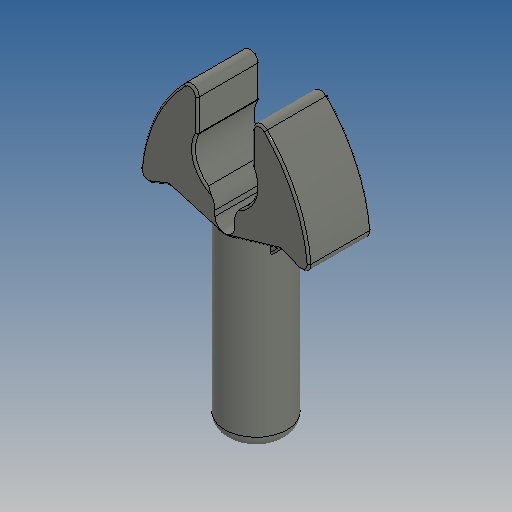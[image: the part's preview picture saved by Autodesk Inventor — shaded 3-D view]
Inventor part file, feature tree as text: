
AUTODESK INVENTOR PART (.ipt)
format: ipt  version: 2025 (Build 290162010, 162A)  size: 288,256 bytes
history: native  units: in
note: dims shown in document units (in); Inventor stores cm internally (conversion verified against a paired STEP export)
features: extrude x3, sketch x2, plane x1, fillet x1
ambient origin geometry x8: Origin, YZ Plane, XZ Plane, XY Plane, X Axis, Y Axis, Z Axis, Center Point
bodies: Solid1 (feature_tree)
feature tree (7):
  sketch  "Sketch1"  dims[d0=0.126in d1=0.1102in]
  extrude  "Extrusion1"  Depth=0.1102in
  extrude  "Extrusion2"  Depth=0.0039in
  plane  "Work Plane1"
  extrude  "Extrusion3"  Depth=0.0039in
  fillet  "Fillet1"  Radius=0.3425in
  sketch  "Sketch2"  dims[d2=0.0157in d3=0.2283in d4=0.0315in d5=0.3425in d6=0.0394in d9=0.0039in d10=0.0945in d11=0.2205in d12=0.1969in d13=0.2244in d14=0.315in d15=0.5906in d16=0.1181in d17=0.126in d18=0.0in d19=0.0551in d20=0.0in d21=0.126in d22=0.0551in d23=0.0in d24=0.0157in d25=0.0394in d26=0.0236in d27=0.0039in]
